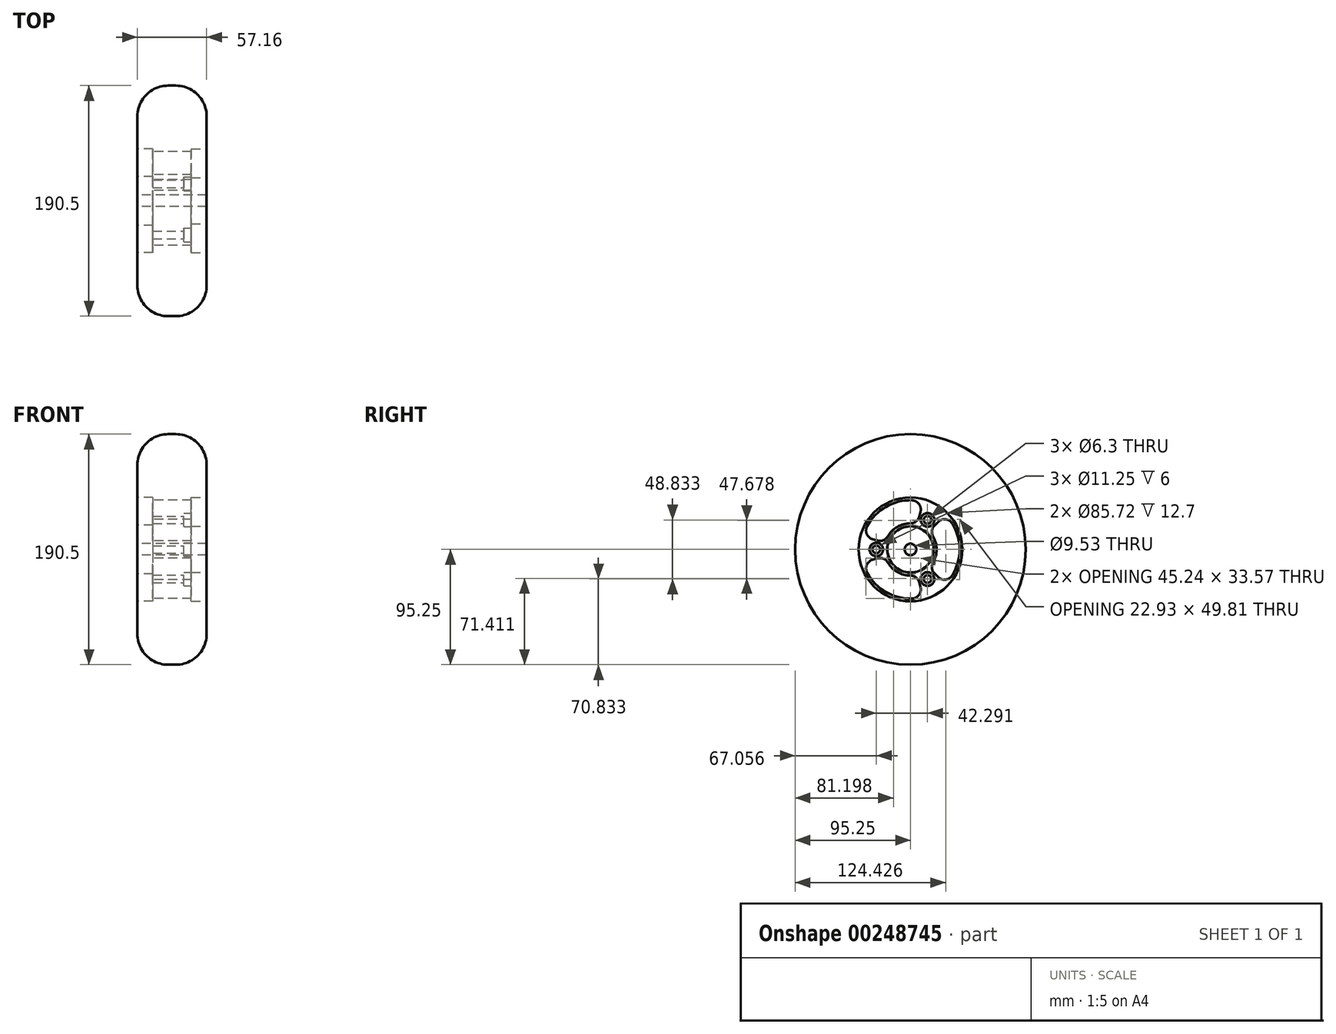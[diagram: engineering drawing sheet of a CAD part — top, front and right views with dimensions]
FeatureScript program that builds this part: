
annotation { "Feature Type Name" : "Feature", "Feature Type Description" : "" }
export const myFeature = defineFeature(function(context is Context, id is Id, definition is map)
    precondition{}
    {
        {
            var Q0;
            Q0=qCreatedBy(makeId("Front.planeOp"),FACE);
            var sketch = newSketch(context, id + "F0", { "sketchPlane" : qUnion([Q0])});
            skLineSegment(sketch, "E0", {"start": v(-143.53, 0) * mm, "end": v(182.55, 0) * mm, "construction": true});
            skLineSegment(sketch, "E1", {"start": v(-28.57, 4.76) * mm, "end": v(-28.57, 69.85) * mm});
            skLineSegment(sketch, "E2", {"start": v(-3.18, 95.25) * mm, "end": v(3.17, 95.25) * mm});
            skLineSegment(sketch, "E3", {"start": v(28.58, 69.85) * mm, "end": v(28.58, 4.76) * mm});
            skLineSegment(sketch, "E4", {"start": v(28.58, 4.76) * mm, "end": v(-28.58, 4.76) * mm});
            skPoint(sketch, "E5.visualSharp", {"position": v(-28.57, 95.25) * mm});
            skArc(sketch, "E5.filletArc", {"start": v(-3.18, 95.25) * mm, "mid": v(-21.14, 87.81) * mm, "end": v(-28.58, 69.85) * mm});
            skPoint(sketch, "E6.visualSharp", {"position": v(28.58, 95.25) * mm});
            skArc(sketch, "E6.filletArc", {"start": v(28.58, 69.85) * mm, "mid": v(21.14, 87.81) * mm, "end": v(3.17, 95.25) * mm});
            skSolve(sketch);
        }
        {
            var Q0;
            Q0 = qSketchRegion(id + "F0", true);
            var Q1;
            Q1=sQuery(id+"F0.wireOp",EDGE,"E0");
            revolve(context, id + "F1", {"entities" : qUnion([Q0]), "axis" : qUnion([Q1]), "revolveType" : RevolveType.FULL});
        }
        {
            var Q0;
            Q0=makeQuery(id+"F1.opRevolve","SWEPT_FACE",FACE,{"disambiguationData":[OSD([sQuery(id+"F0.wireOp",EDGE,"E3")])]});
            var sketch = newSketch(context, id + "F2", { "sketchPlane" : qUnion([Q0])});
            skCircle(sketch, "E7", {"center": v(0, 0) * mm, "radius": 42.86 * mm});
            skCircle(sketch, "E8", {"center": v(0, 0) * mm, "radius": 19.05 * mm});
            skSolve(sketch);
        }
        {
            var Q0;
            Q0 = qSketchRegion(id + "F2", true);
            extrude(context, id + "F3", {"entities" : qUnion([Q0]), "operationType" : NewBodyOperationType.REMOVE, "oppositeDirection" : true, "depth" : 12.7 * mm});
        }
        {
            var Q0;
            Q0=makeQuery(id+"F1.opRevolve","SWEPT_FACE",FACE,{"disambiguationData":[OSD([sQuery(id+"F0.wireOp",EDGE,"E1")])]});
            var sketch = newSketch(context, id + "F4", { "sketchPlane" : qUnion([Q0])});
            skCircle(sketch, "E9", {"center": v(0, 0) * mm, "radius": 42.86 * mm});
            skCircle(sketch, "E10", {"center": v(0, 0) * mm, "radius": 20.2 * mm});
            skSolve(sketch);
        }
        {
            var Q0;
            Q0 = qSketchRegion(id + "F4", true);
            extrude(context, id + "F5", {"entities" : qUnion([Q0]), "operationType" : NewBodyOperationType.REMOVE, "oppositeDirection" : true, "depth" : 12.7 * mm});
        }
        {
            var Q0;
            Q0=makeQuery(id+"F5.boolean.opBoolean","COPY",FACE,{"derivedFrom":makeQuery(id+"F5.opExtrude","CAP_FACE",FACE,{"disambiguationData":[OSD([sQuery(id+"F4.wireOp",EDGE,"E9"),sQuery(id+"F4.wireOp",EDGE,"E10")])],"isStart":false})});
            var sketch = newSketch(context, id + "F6", { "sketchPlane" : qUnion([Q0])});
            skLineSegment(sketch, "E11", {"start": v(0, 0) * mm, "end": v(-190.7, 0) * mm, "construction": true});
            skArc(sketch, "E12", {"start": v(-18.72, 10.76) * mm, "mid": v(-21.6, 0) * mm, "end": v(-18.72, -10.76) * mm});
            skArc(sketch, "E13", {"start": v(-34.6, 21.33) * mm, "mid": v(-40.64, 0) * mm, "end": v(-34.6, -21.33) * mm});
            skLineSegment(sketch, "E14", {"start": v(-19.94, 19.94) * mm, "end": v(-22.72, 22.72) * mm});
            skLineSegment(sketch, "E15", {"start": v(-19.94, -19.94) * mm, "end": v(-22.72, -22.72) * mm});
            skPoint(sketch, "E16.visualSharp", {"position": v(-28.74, -28.74) * mm});
            skArc(sketch, "E16.filletArc", {"start": v(-34.6, -21.33) * mm, "mid": v(-29, -24.9) * mm, "end": v(-22.72, -22.72) * mm});
            skPoint(sketch, "E17.visualSharp", {"position": v(-15.27, -15.27) * mm});
            skArc(sketch, "E17.filletArc", {"start": v(-19.94, -19.94) * mm, "mid": v(-17.77, -15.55) * mm, "end": v(-18.72, -10.76) * mm});
            skPoint(sketch, "E18.visualSharp", {"position": v(-15.27, 15.27) * mm});
            skArc(sketch, "E18.filletArc", {"start": v(-18.72, 10.76) * mm, "mid": v(-17.77, 15.55) * mm, "end": v(-19.94, 19.94) * mm});
            skPoint(sketch, "E19.visualSharp", {"position": v(-28.74, 28.74) * mm});
            skArc(sketch, "E19.filletArc", {"start": v(-22.72, 22.72) * mm, "mid": v(-29, 24.9) * mm, "end": v(-34.6, 21.33) * mm});
            skPoint(sketch, "E20.1.0", {"position": v(-10.52, -39.26) * mm});
            skArc(sketch, "E20.1.1", {"start": v(-1.18, -40.62) * mm, "mid": v(20.32, -35.2) * mm, "end": v(35.77, -19.3) * mm});
            skArc(sketch, "E20.1.2", {"start": v(35.77, -19.3) * mm, "mid": v(36.06, -12.66) * mm, "end": v(31.03, -8.32) * mm});
            skPoint(sketch, "E20.1.3", {"position": v(20.85, -5.59) * mm});
            skArc(sketch, "E20.1.4", {"start": v(0.05, -21.59) * mm, "mid": v(10.8, -18.7) * mm, "end": v(18.67, -10.83) * mm});
            skPoint(sketch, "E20.1.5", {"position": v(-5.59, -20.85) * mm});
            skArc(sketch, "E20.1.6", {"start": v(27.24, -7.3) * mm, "mid": v(22.36, -7.62) * mm, "end": v(18.67, -10.83) * mm});
            skArc(sketch, "E20.1.7", {"start": v(0.05, -21.59) * mm, "mid": v(-4.58, -23.17) * mm, "end": v(-7.3, -27.24) * mm});
            skArc(sketch, "E20.1.8", {"start": v(-8.32, -31.03) * mm, "mid": v(-7.07, -37.56) * mm, "end": v(-1.18, -40.62) * mm});
            skLineSegment(sketch, "E20.1.9", {"start": v(-7.3, -27.24) * mm, "end": v(-8.32, -31.03) * mm});
            skLineSegment(sketch, "E20.1.10", {"start": v(27.24, -7.3) * mm, "end": v(31.03, -8.32) * mm});
            skPoint(sketch, "E20.2.0", {"position": v(39.26, 10.52) * mm});
            skArc(sketch, "E20.2.1", {"start": v(35.77, 19.3) * mm, "mid": v(20.32, 35.2) * mm, "end": v(-1.18, 40.62) * mm});
            skArc(sketch, "E20.2.2", {"start": v(-1.18, 40.62) * mm, "mid": v(-7.07, 37.56) * mm, "end": v(-8.32, 31.03) * mm});
            skPoint(sketch, "E20.2.3", {"position": v(-5.59, 20.85) * mm});
            skArc(sketch, "E20.2.4", {"start": v(18.67, 10.83) * mm, "mid": v(10.8, 18.7) * mm, "end": v(0.05, 21.59) * mm});
            skPoint(sketch, "E20.2.5", {"position": v(20.85, 5.59) * mm});
            skArc(sketch, "E20.2.6", {"start": v(-7.3, 27.24) * mm, "mid": v(-4.58, 23.17) * mm, "end": v(0.05, 21.59) * mm});
            skArc(sketch, "E20.2.7", {"start": v(18.67, 10.83) * mm, "mid": v(22.36, 7.62) * mm, "end": v(27.24, 7.3) * mm});
            skArc(sketch, "E20.2.8", {"start": v(31.03, 8.32) * mm, "mid": v(36.06, 12.66) * mm, "end": v(35.77, 19.3) * mm});
            skLineSegment(sketch, "E20.2.9", {"start": v(27.24, 7.3) * mm, "end": v(31.03, 8.32) * mm});
            skLineSegment(sketch, "E20.2.10", {"start": v(-7.3, 27.24) * mm, "end": v(-8.32, 31.03) * mm});
            skSolve(sketch);
        }
        {
            var Q0;
            Q0 = qSketchRegion(id + "F6", true);
            extrude(context, id + "F7", {"entities" : qUnion([Q0]), "operationType" : NewBodyOperationType.REMOVE, "endBound" : BoundingType.THROUGH_ALL, "oppositeDirection" : true, "depth" : 25.4 * mm});
        }
        {
            var Q0;
            Q0=makeQuery(id+"F3.boolean.opBoolean","COPY",FACE,{"derivedFrom":makeQuery(id+"F3.opExtrude","CAP_FACE",FACE,{"disambiguationData":[OSD([sQuery(id+"F2.wireOp",EDGE,"E7"),sQuery(id+"F2.wireOp",EDGE,"E8")])],"isStart":false})});
            var sketch = newSketch(context, id + "F8", { "sketchPlane" : qUnion([Q0])});
            skCircle(sketch, "E21", {"center": v(-28.2, 0) * mm, "radius": 5.46 * mm, "construction": true});
            skPoint(sketch, "E22.1.0", {"position": v(14.1, -24.42) * mm});
            skPoint(sketch, "E22.2.0", {"position": v(14.1, 24.42) * mm});
            skPoint(sketch, "E22.center", {"position": v(0, 0) * mm});
            skSolve(sketch);
        }
        {
            var Q0;
            Q0=sQuery(id+"F8.wireOp",VERTEX,"E22.1.0");
            var Q1;
            Q1=sQuery(id+"F8.wireOp",VERTEX,"E22.2.0");
            var Q2;
            Q2=sQuery(id+"F8.wireOp",VERTEX,"E21.center");
            var Q3;
            Q3=makeQuery(id+"F1.opRevolve","SWEPT_BODY",BODY,{"disambiguationData":[OSD([sQuery(id+"F0.wireOp",EDGE,"E1"),sQuery(id+"F0.wireOp",EDGE,"E2"),sQuery(id+"F0.wireOp",EDGE,"E3"),sQuery(id+"F0.wireOp",EDGE,"E4"),sQuery(id+"F0.wireOp",EDGE,"E5.filletArc"),sQuery(id+"F0.wireOp",EDGE,"E6.filletArc")])]});
            hole(context, id + "F9", {"style" : HoleStyle.C_BORE, "endStyle" : HoleEndStyle.THROUGH, "standardTappedOrClearance" : lookupTablePath({ "standard" : "ISO", "fit" : "Close", "size" : "M6", "type" : "Clearance" }), "standardBlindInLast" : lookupTablePath({ "fit" : "Close", "standard" : "ISO", "size" : "M6", "type" : "Clearance" }), "holeDiameter" : 6.3 * mm, "cBoreDiameter" : 11.25 * mm, "cBoreDepth" : 6 * mm, "tappedDepth" : 12.7 * mm, "tapClearance" : 3, "startFromSketch" : true, "locations" : qUnion([Q0, Q1, Q2]), "scope" : qUnion([Q3])});
        }
    });
